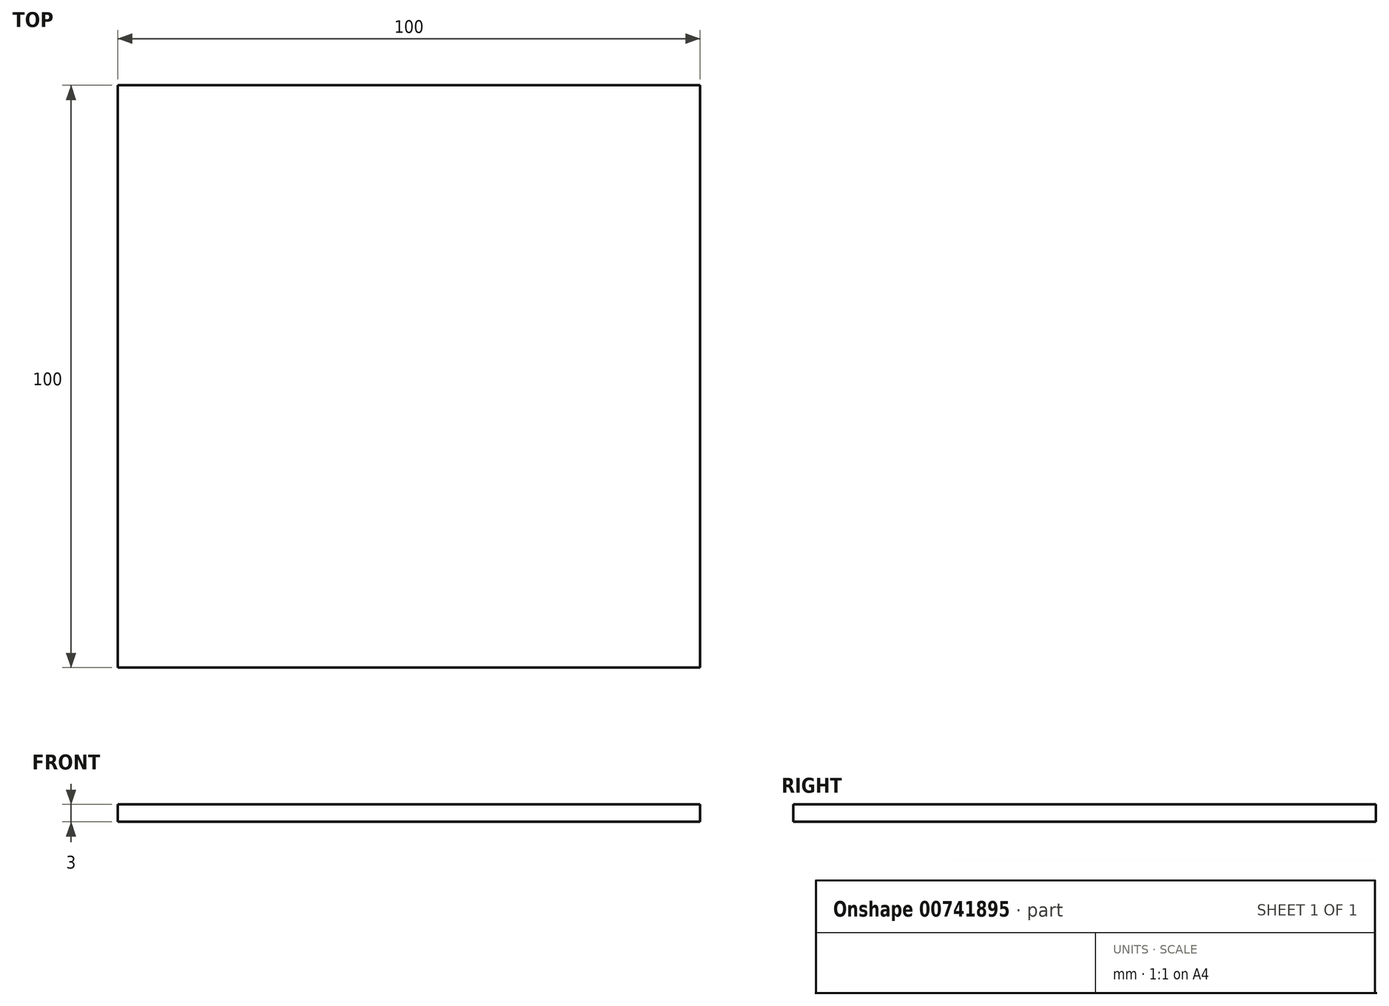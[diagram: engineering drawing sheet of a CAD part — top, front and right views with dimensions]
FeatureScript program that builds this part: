
annotation { "Feature Type Name" : "Feature", "Feature Type Description" : "" }
export const myFeature = defineFeature(function(context is Context, id is Id, definition is map)
    precondition{}
    {
        {
            var Q0;
            Q0=qCreatedBy(makeId("Top.planeOp"),FACE);
            var sketch = newSketch(context, id + "F0", { "sketchPlane" : qUnion([Q0])});
            skLineSegment(sketch, "E0.bottom", {"start": v(-50, 50) * mm, "end": v(50, 50) * mm});
            skLineSegment(sketch, "E0.top", {"start": v(-50, -50) * mm, "end": v(50, -50) * mm});
            skLineSegment(sketch, "E0.left", {"start": v(-50, 50) * mm, "end": v(-50, -50) * mm});
            skLineSegment(sketch, "E0.right", {"start": v(50, 50) * mm, "end": v(50, -50) * mm});
            skSolve(sketch);
        }
        {
            var Q0;
            Q0 = qSketchRegion(id + "F0", true);
            extrude(context, id + "F1", {"entities" : qUnion([Q0]), "depth" : 3 * mm, "offsetDistance" : 25 * mm});
        }
    });
